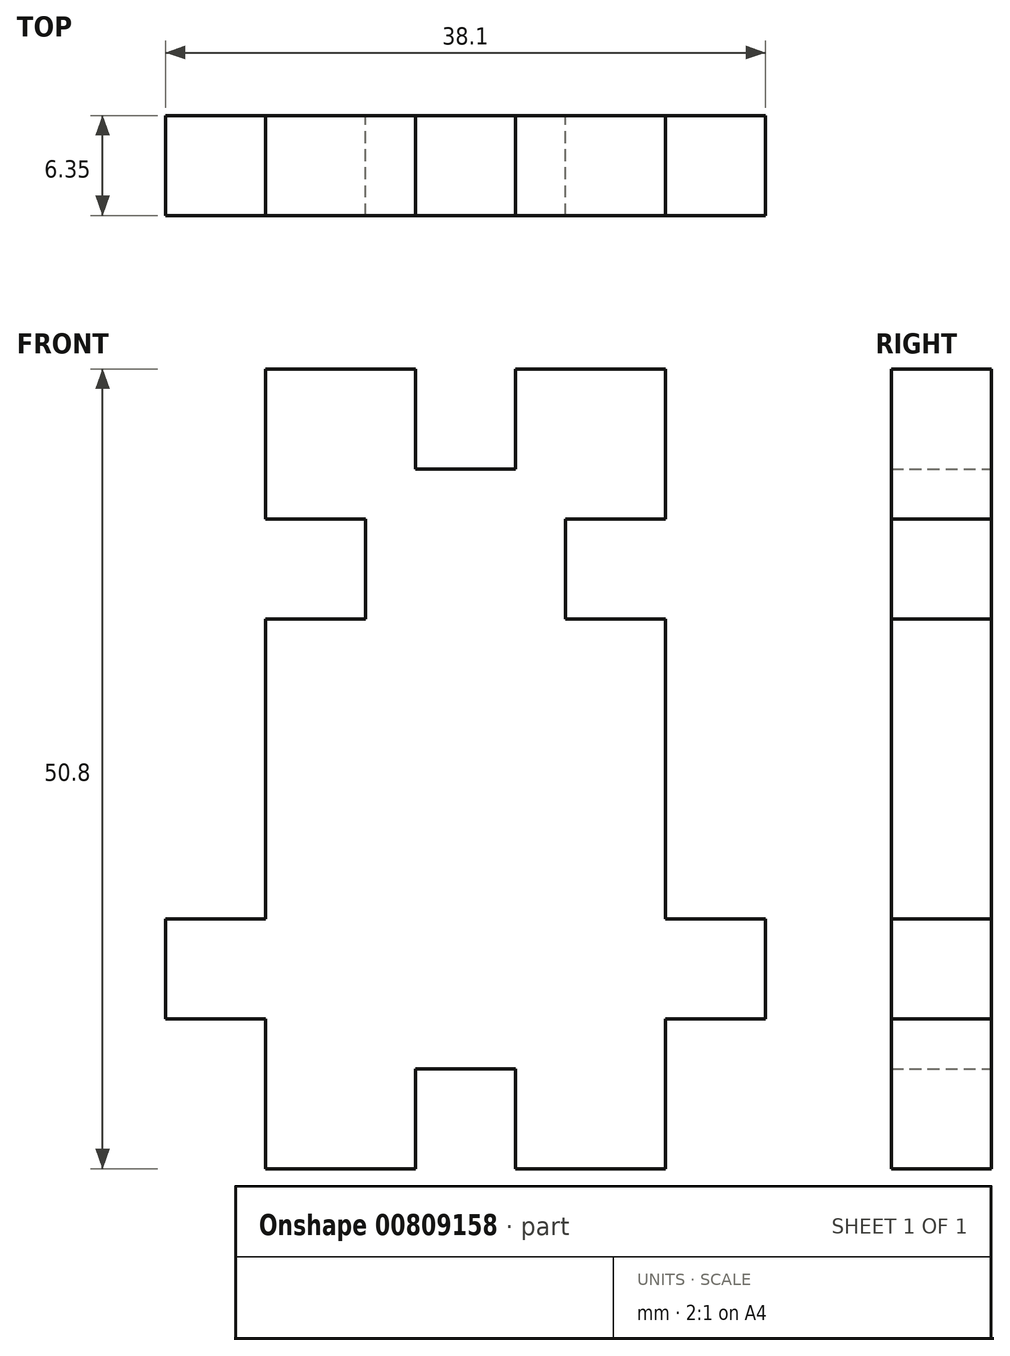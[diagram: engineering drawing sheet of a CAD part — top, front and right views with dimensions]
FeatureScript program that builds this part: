
annotation { "Feature Type Name" : "Feature", "Feature Type Description" : "" }
export const myFeature = defineFeature(function(context is Context, id is Id, definition is map)
    precondition{}
    {
        {
            var Q0;
            Q0=qCreatedBy(makeId("Front.planeOp"),FACE);
            var sketch = newSketch(context, id + "F0", { "sketchPlane" : qUnion([Q0])});
            skLineSegment(sketch, "E0", {"start": v(-3.18, 25.4) * mm, "end": v(-12.7, 25.4) * mm});
            skLineSegment(sketch, "E1", {"start": v(-12.7, 25.4) * mm, "end": v(-3.18, 25.4) * mm});
            skLineSegment(sketch, "E2", {"start": v(-12.7, 25.4) * mm, "end": v(-12.7, 15.88) * mm});
            skLineSegment(sketch, "E3", {"start": v(-12.7, -25.4) * mm, "end": v(-3.18, -25.4) * mm});
            skLineSegment(sketch, "E4.MirrorCS", {"start": v(12.7, 25.4) * mm, "end": v(3.18, 25.4) * mm});
            skLineSegment(sketch, "E5.MirrorCS", {"start": v(12.7, 25.4) * mm, "end": v(12.7, 15.87) * mm});
            skLineSegment(sketch, "E6.MirrorCS", {"start": v(12.7, -25.4) * mm, "end": v(3.18, -25.4) * mm});
            skLineSegment(sketch, "E7", {"start": v(-3.17, 25.4) * mm, "end": v(-3.17, 19.05) * mm});
            skLineSegment(sketch, "E8", {"start": v(-3.17, 19.05) * mm, "end": v(3.17, 19.05) * mm});
            skLineSegment(sketch, "E9", {"start": v(3.17, 25.4) * mm, "end": v(3.17, 19.05) * mm});
            skPoint(sketch, "E10.orphan", {"position": v(0, 25.4) * mm});
            skLineSegment(sketch, "E11", {"start": v(-12.7, 0) * mm, "end": v(-12.7, 9.53) * mm});
            skLineSegment(sketch, "E12", {"start": v(-12.7, 15.87) * mm, "end": v(-6.35, 15.88) * mm});
            skLineSegment(sketch, "E13", {"start": v(-6.35, 15.88) * mm, "end": v(-6.35, 9.53) * mm});
            skLineSegment(sketch, "E14", {"start": v(-12.7, 9.52) * mm, "end": v(-6.35, 9.52) * mm});
            skLineSegment(sketch, "E15.trimOffspring", {"start": v(-12.7, 9.53) * mm, "end": v(-12.7, -9.52) * mm});
            skLineSegment(sketch, "E16.trimOffspring", {"start": v(-12.7, 15.87) * mm, "end": v(-12.7, 25.4) * mm});
            skPoint(sketch, "E17.start.orphan", {"position": v(-12.7, 12.7) * mm});
            skLineSegment(sketch, "E18", {"start": v(-12.7, 0) * mm, "end": v(-12.7, -9.52) * mm});
            skLineSegment(sketch, "E19", {"start": v(-12.7, -9.52) * mm, "end": v(-19.05, -9.52) * mm});
            skLineSegment(sketch, "E20", {"start": v(-19.05, -9.52) * mm, "end": v(-19.05, -15.87) * mm});
            skLineSegment(sketch, "E21", {"start": v(-12.7, -15.87) * mm, "end": v(-19.05, -15.87) * mm});
            skLineSegment(sketch, "E22.trimOffspring", {"start": v(-12.7, -15.87) * mm, "end": v(-12.7, -25.4) * mm});
            skPoint(sketch, "E23.start.orphan", {"position": v(-12.7, -12.7) * mm});
            skLineSegment(sketch, "E24", {"start": v(-3.18, -25.4) * mm, "end": v(-3.18, -19.05) * mm});
            skLineSegment(sketch, "E25", {"start": v(-3.18, -19.05) * mm, "end": v(3.17, -19.05) * mm});
            skLineSegment(sketch, "E26", {"start": v(3.17, -25.4) * mm, "end": v(3.17, -19.05) * mm});
            skPoint(sketch, "E27.orphan", {"position": v(0, -25.4) * mm});
            skLineSegment(sketch, "E28.MirrorCS", {"start": v(12.7, -15.87) * mm, "end": v(19.05, -15.87) * mm});
            skLineSegment(sketch, "E29.MirrorCS", {"start": v(12.7, -9.52) * mm, "end": v(19.05, -9.52) * mm});
            skLineSegment(sketch, "E30.MirrorCS", {"start": v(19.05, -9.52) * mm, "end": v(19.05, -15.87) * mm});
            skLineSegment(sketch, "E31.trimOffspring", {"start": v(12.7, -15.87) * mm, "end": v(12.7, -25.4) * mm});
            skPoint(sketch, "E32.start.orphan", {"position": v(0, 0) * mm});
            skLineSegment(sketch, "E33.MirrorCS", {"start": v(12.7, 15.87) * mm, "end": v(6.35, 15.88) * mm});
            skLineSegment(sketch, "E34.MirrorCS", {"start": v(6.35, 15.88) * mm, "end": v(6.35, 9.53) * mm});
            skLineSegment(sketch, "E35.MirrorCS", {"start": v(12.7, 9.52) * mm, "end": v(6.35, 9.52) * mm});
            skPoint(sketch, "E36.end.orphan", {"position": v(0, 19.05) * mm});
            skLineSegment(sketch, "E37.trimOffspring", {"start": v(12.7, 9.52) * mm, "end": v(12.7, -9.52) * mm});
            skSolve(sketch);
        }
        {
            var Q0;
            Q0 = qSketchRegion(id + "F0", true);
            extrude(context, id + "F1", {"entities" : qUnion([Q0]), "depth" : 6.35 * mm, "offsetDistance" : 25.4 * mm});
        }
    });
